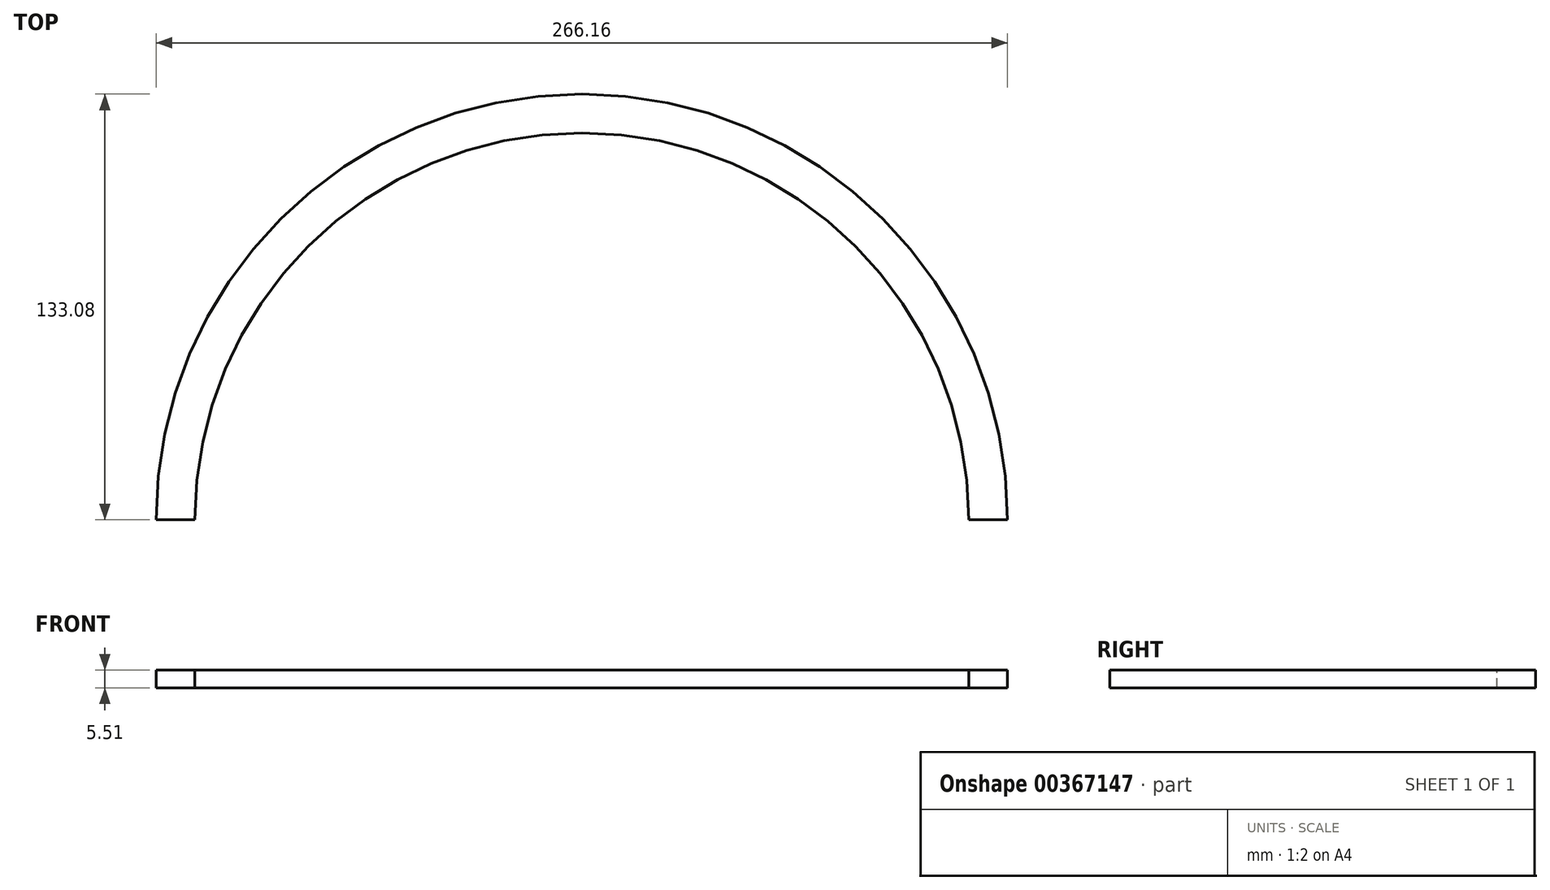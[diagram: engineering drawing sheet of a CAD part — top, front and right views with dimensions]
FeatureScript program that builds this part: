
annotation { "Feature Type Name" : "Feature", "Feature Type Description" : "" }
export const myFeature = defineFeature(function(context is Context, id is Id, definition is map)
    precondition{}
    {
        {
            var Q0;
            Q0=qCreatedBy(makeId("Top.planeOp"),FACE);
            var sketch = newSketch(context, id + "F0", { "sketchPlane" : qUnion([Q0])});
            skArc(sketch, "E0", {"start": v(127, 0) * mm, "mid": v(0, 127) * mm, "end": v(-127, 0) * mm});
            skArc(sketch, "E1", {"start": v(131.5, 0) * mm, "mid": v(0, 131.5) * mm, "end": v(-131.5, 0) * mm});
            skArc(sketch, "E2", {"start": v(122.5, 0) * mm, "mid": v(0, 122.5) * mm, "end": v(-122.5, 0) * mm});
            skArc(sketch, "E3.0", {"start": v(133.08, 0) * mm, "mid": v(0, 133.08) * mm, "end": v(-133.08, 0) * mm});
            skArc(sketch, "E4.0", {"start": v(120.92, 0) * mm, "mid": v(0, 120.92) * mm, "end": v(-120.92, 0) * mm});
            skLineSegment(sketch, "E5", {"start": v(-133.08, 0) * mm, "end": v(133.08, 0) * mm});
            skSolve(sketch);
        }
        {
            var Q0;
            {var subQ0=sQuery(id+"F0.wireOp",EDGE,"E0");Q0=makeQuery(id+"F0.imprint","IMPRINT",FACE,{"disambiguationData":[TD([[makeQuery(id+"F0.imprint","IMPRINT",EDGE,{"derivedFrom":subQ0}),-1.0]])]});}
            var Q1;
            {var subQ0=sQuery(id+"F0.wireOp",EDGE,"E0");Q1=makeQuery(id+"F0.imprint","IMPRINT",FACE,{"disambiguationData":[TD([[makeQuery(id+"F0.imprint","IMPRINT",EDGE,{"derivedFrom":subQ0}),1.0]])]});}
            var Q2;
            {var subQ0=sQuery(id+"F0.wireOp",EDGE,"E1");Q2=makeQuery(id+"F0.imprint","IMPRINT",FACE,{"disambiguationData":[TD([[makeQuery(id+"F0.imprint","IMPRINT",EDGE,{"derivedFrom":subQ0}),-1.0]])]});}
            var Q3;
            {var subQ0=sQuery(id+"F0.wireOp",EDGE,"E2");Q3=makeQuery(id+"F0.imprint","IMPRINT",FACE,{"disambiguationData":[TD([[makeQuery(id+"F0.imprint","IMPRINT",EDGE,{"derivedFrom":subQ0}),1.0]])]});}
            extrude(context, id + "F1", {"entities" : qUnion([Q0, Q1, Q2, Q3]), "oppositeDirection" : true, "depth" : 5.5 * mm});
        }
    });
